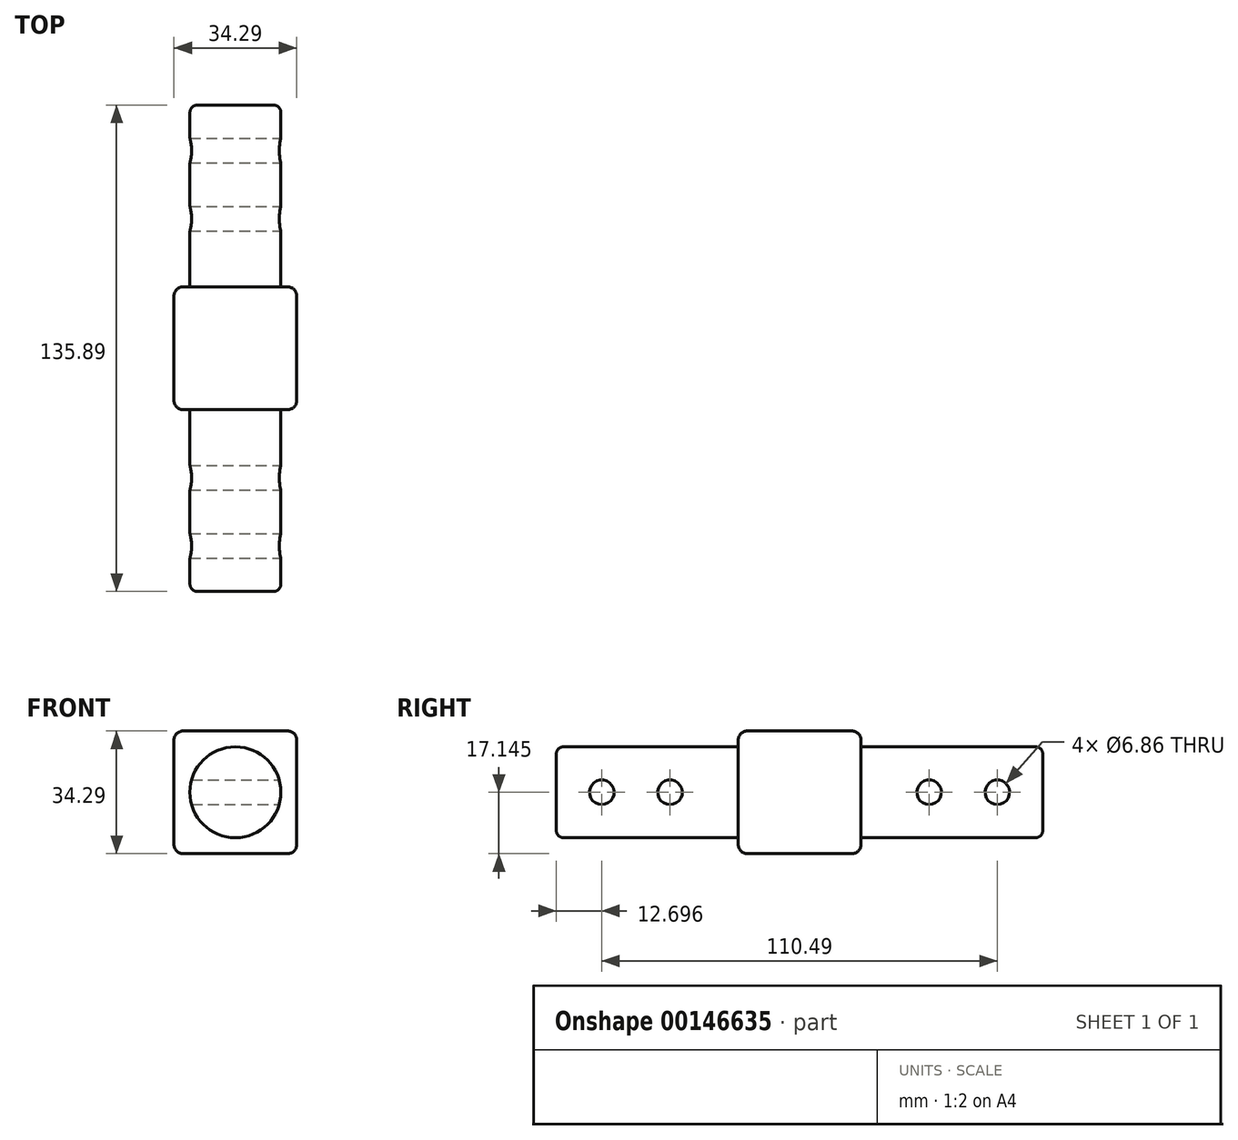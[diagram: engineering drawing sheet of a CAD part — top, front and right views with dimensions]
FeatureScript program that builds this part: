
annotation { "Feature Type Name" : "Feature", "Feature Type Description" : "" }
export const myFeature = defineFeature(function(context is Context, id is Id, definition is map)
    precondition{}
    {
        {
            var Q0;
            Q0=qCreatedBy(makeId("Top.planeOp"),FACE);
            var sketch = newSketch(context, id + "F0", { "sketchPlane" : qUnion([Q0])});
            skLineSegment(sketch, "E0.bottom", {"start": v(-13.47, 23.7) * mm, "end": v(20.82, 23.7) * mm});
            skLineSegment(sketch, "E0.top", {"start": v(-13.47, -10.58) * mm, "end": v(20.82, -10.58) * mm});
            skLineSegment(sketch, "E0.left", {"start": v(-13.47, 23.7) * mm, "end": v(-13.47, -10.58) * mm});
            skLineSegment(sketch, "E0.right", {"start": v(20.82, 23.7) * mm, "end": v(20.82, -10.58) * mm});
            skSolve(sketch);
        }
        {
            var Q0;
            Q0=qSketchRegion(id+"F0",true);
            extrude(context, id + "F1", {"entities" : qUnion([Q0]), "depth" : 34.3 * mm});
        }
        {
            var Q0;
            Q0=makeQuery(id+"F1.opExtrude","SWEPT_FACE",FACE,{"disambiguationData":[OSD([sQuery(id+"F0.wireOp",EDGE,"E0.top")])]});
            var sketch = newSketch(context, id + "F3", { "sketchPlane" : qUnion([Q0])});
            skLineSegment(sketch, "E1", {"start": v(-13.47, 17.15) * mm, "end": v(24.43, 17.15) * mm, "construction": true});
            skLineSegment(sketch, "E2", {"start": v(3.67, 0) * mm, "end": v(3.67, 34.3) * mm, "construction": true});
            skCircle(sketch, "E3", {"center": v(3.67, 17.15) * mm, "radius": 12.7 * mm});
            skSolve(sketch);
        }
        {
            var Q0;
            Q0=qSketchRegion(id+"F3",true);
            extrude(context, id + "F4", {"entities" : qUnion([Q0]), "operationType" : NewBodyOperationType.ADD, "depth" : 50.8 * mm});
        }
        {
            var Q0;
            Q0=qCreatedBy(makeId("Front.planeOp"),FACE);
            var sketch = newSketch(context, id + "F5", { "sketchPlane" : qUnion([Q0])});
            skCircle(sketch, "E4", {"center": v(3.67, 53.34) * mm, "radius": 3.43 * mm});
            skCircle(sketch, "E5", {"center": v(3.67, 72.4) * mm, "radius": 3.43 * mm});
            skSolve(sketch);
        }
        {
            var Q0;
            Q0=qSketchRegion(id+"F5",true);
            extrude(context, id + "F6", {"entities" : qUnion([Q0]), "operationType" : NewBodyOperationType.REMOVE, "endBound" : BoundingType.SYMMETRIC, "oppositeDirection" : true, "depth" : 50.8 * mm});
        }
        {
            var Q0;
            Q0=qCreatedBy(makeId("Right.planeOp"),FACE);
            var sketch = newSketch(context, id + "F7", { "sketchPlane" : qUnion([Q0])});
            skCircle(sketch, "E6", {"center": v(-29.63, 17.15) * mm, "radius": 3.43 * mm});
            skCircle(sketch, "E7", {"center": v(-48.68, 17.15) * mm, "radius": 3.43 * mm});
            skSolve(sketch);
        }
        {
            var Q0;
            Q0=qSketchRegion(id+"F7",true);
            extrude(context, id + "F8", {"entities" : qUnion([Q0]), "operationType" : NewBodyOperationType.REMOVE, "endBound" : BoundingType.SYMMETRIC, "oppositeDirection" : true, "depth" : 50.8 * mm});
        }
        {
            var Q0;
            Q0=qCreatedBy(makeId("Front.planeOp"),FACE);
            var sketch = newSketch(context, id + "F9", { "sketchPlane" : qUnion([Q0])});
            skCircle(sketch, "E8", {"center": v(-51.57, 17.15) * mm, "radius": 3.43 * mm});
            skCircle(sketch, "E9", {"center": v(-32.52, 17.15) * mm, "radius": 3.43 * mm});
            skSolve(sketch);
        }
        {
            var Q0;
            Q0=qSketchRegion(id+"F9",true);
            extrude(context, id + "F10", {"entities" : qUnion([Q0]), "operationType" : NewBodyOperationType.REMOVE, "endBound" : BoundingType.SYMMETRIC, "oppositeDirection" : true, "depth" : 50.8 * mm});
        }
        {
            var Q0;
            Q0=makeQuery(id+"F1.opExtrude","SWEPT_EDGE",EDGE,{"disambiguationData":[OSD([sQuery(id+"F0.wireOp",EDGE,"E0.bottom"),sQuery(id+"F0.wireOp",EDGE,"E0.right")])]});
            var Q1;
            Q1=makeQuery(id+"F1.opExtrude","CAP_EDGE",EDGE,{"disambiguationData":[OSD([sQuery(id+"F0.wireOp",EDGE,"E0.right")])],"isStart":false});
            var Q2;
            Q2=makeQuery(id+"F1.opExtrude","SWEPT_EDGE",EDGE,{"disambiguationData":[OSD([sQuery(id+"F0.wireOp",EDGE,"E0.top"),sQuery(id+"F0.wireOp",EDGE,"E0.right")])]});
            var Q3;
            Q3=makeQuery(id+"F1.opExtrude","CAP_EDGE",EDGE,{"disambiguationData":[OSD([sQuery(id+"F0.wireOp",EDGE,"E0.right")])],"isStart":true});
            var Q4;
            Q4=makeQuery(id+"F1.opExtrude","CAP_EDGE",EDGE,{"disambiguationData":[OSD([sQuery(id+"F0.wireOp",EDGE,"E0.bottom")])],"isStart":true});
            var Q5;
            Q5=makeQuery(id+"F1.opExtrude","CAP_EDGE",EDGE,{"disambiguationData":[OSD([sQuery(id+"F0.wireOp",EDGE,"E0.bottom")])],"isStart":false});
            var Q6;
            Q6=makeQuery(id+"F1.opExtrude","SWEPT_EDGE",EDGE,{"disambiguationData":[OSD([sQuery(id+"F0.wireOp",EDGE,"E0.bottom"),sQuery(id+"F0.wireOp",EDGE,"E0.left")])]});
            var Q7;
            Q7=makeQuery(id+"F1.opExtrude","CAP_EDGE",EDGE,{"disambiguationData":[OSD([sQuery(id+"F0.wireOp",EDGE,"E0.left")])],"isStart":true});
            var Q8;
            Q8=makeQuery(id+"F1.opExtrude","CAP_EDGE",EDGE,{"disambiguationData":[OSD([sQuery(id+"F0.wireOp",EDGE,"E0.top")])],"isStart":true});
            var Q9;
            Q9=makeQuery(id+"F1.opExtrude","CAP_EDGE",EDGE,{"disambiguationData":[OSD([sQuery(id+"F0.wireOp",EDGE,"E0.left")])],"isStart":false});
            var Q10;
            Q10=makeQuery(id+"F1.opExtrude","SWEPT_EDGE",EDGE,{"disambiguationData":[OSD([sQuery(id+"F0.wireOp",EDGE,"E0.top"),sQuery(id+"F0.wireOp",EDGE,"E0.left")])]});
            var Q11;
            Q11=makeQuery(id+"F1.opExtrude","CAP_EDGE",EDGE,{"disambiguationData":[OSD([sQuery(id+"F0.wireOp",EDGE,"E0.top")])],"isStart":false});
            fillet(context, id + "F11", {"entities" : qUnion([Q0, Q1, Q2, Q3, Q4, Q5, Q6, Q7, Q8, Q9, Q10, Q11]), "radius" : 2.54 * mm, "tangentPropagation" : true, "allowEdgeOverflow" : false});
        }
        {
            var Q0;
            Q0=makeQuery(id+"F1.opExtrude","SWEPT_FACE",FACE,{"disambiguationData":[OSD([sQuery(id+"F0.wireOp",EDGE,"E0.bottom")])]});
            var sketch = newSketch(context, id + "F12", { "sketchPlane" : qUnion([Q0])});
            skLineSegment(sketch, "E10", {"start": v(-18.28, 17.15) * mm, "end": v(4.82, 17.15) * mm, "construction": true});
            skPoint(sketch, "E10.endSnap0", {"position": v(-18.28, 17.15) * mm});
            skLineSegment(sketch, "E11", {"start": v(-3.67, 31.75) * mm, "end": v(-3.67, 14.65) * mm, "construction": true});
            skCircle(sketch, "E12", {"center": v(-3.67, 17.15) * mm, "radius": 12.7 * mm});
            skSolve(sketch);
        }
        {
            var Q0;
            Q0=qSketchRegion(id+"F12",true);
            extrude(context, id + "F13", {"entities" : qUnion([Q0]), "operationType" : NewBodyOperationType.ADD, "depth" : 50.8 * mm});
        }
        {
            var Q0;
            Q0=qCreatedBy(makeId("Right.planeOp"),FACE);
            var sketch = newSketch(context, id + "F14", { "sketchPlane" : qUnion([Q0])});
            skCircle(sketch, "E13", {"center": v(42.76, 17.15) * mm, "radius": 3.43 * mm});
            skCircle(sketch, "E14", {"center": v(61.8, 17.15) * mm, "radius": 3.43 * mm});
            skSolve(sketch);
        }
        {
            var Q0;
            Q0=qSketchRegion(id+"F14",true);
            extrude(context, id + "F15", {"entities" : qUnion([Q0]), "operationType" : NewBodyOperationType.REMOVE, "endBound" : BoundingType.SYMMETRIC, "oppositeDirection" : true, "depth" : 50.8 * mm});
        }
        {
            var Q0;
            Q0=makeQuery(id+"Ff8LsmKBHV4Uzf6_1.opExtrude","CAP_EDGE",EDGE,{"disambiguationData":[OSD([sQuery(id+"FGSIiZxj4pOu3NG_1.wireOp",EDGE,"UelfSfaY-AMup-COUh-hXSA-o5mW5rKARTS6")])],"isStart":false});
            var Q1;
            Q1=makeQuery(id+"F4.opExtrude","CAP_EDGE",EDGE,{"disambiguationData":[OSD([sQuery(id+"F3.wireOp",EDGE,"E3")])],"isStart":false});
            var Q2;
            Q2=makeQuery(id+"F2.opExtrude","CAP_EDGE",EDGE,{"disambiguationData":[OSD([sQuery(id+"FIc3ZwD0MRkNizU_1.wireOp",EDGE,"5X2wenA0-NZPo-tNKO-rhVc-4ux0vwX6K1N9")])],"isStart":false});
            var Q3;
            Q3=makeQuery(id+"F13.opExtrude","CAP_EDGE",EDGE,{"disambiguationData":[OSD([sQuery(id+"F12.wireOp",EDGE,"E12")])],"isStart":false});
            var Q4;
            Q4=makeQuery(id+"F9gDW6ytOR0zG9s_1.opExtrude","CAP_EDGE",EDGE,{"disambiguationData":[OSD([sQuery(id+"FiyRrB6nUQmxvW3_1.wireOp",EDGE,"TDc28uEK-sT7R-I2aJ-wYcu-fXwbEVHNaGzo")])],"isStart":false});
            fillet(context, id + "F16", {"entities" : qUnion([Q0, Q1, Q2, Q3, Q4]), "radius" : 2.03 * mm, "tangentPropagation" : true, "allowEdgeOverflow" : false});
        }
        {
            var Q0;
            Q0=qCreatedBy(makeId("Front.planeOp"),FACE);
            var sketch = newSketch(context, id + "F17", { "sketchPlane" : qUnion([Q0])});
            skCircle(sketch, "E15", {"center": v(58.92, 17.15) * mm, "radius": 3.43 * mm});
            skCircle(sketch, "E16", {"center": v(39.87, 17.15) * mm, "radius": 3.43 * mm});
            skSolve(sketch);
        }
        {
            var Q0;
            Q0=qSketchRegion(id+"F17",true);
            extrude(context, id + "F18", {"entities" : qUnion([Q0]), "operationType" : NewBodyOperationType.REMOVE, "endBound" : BoundingType.SYMMETRIC, "oppositeDirection" : true, "depth" : 50.8 * mm});
        }
    });
